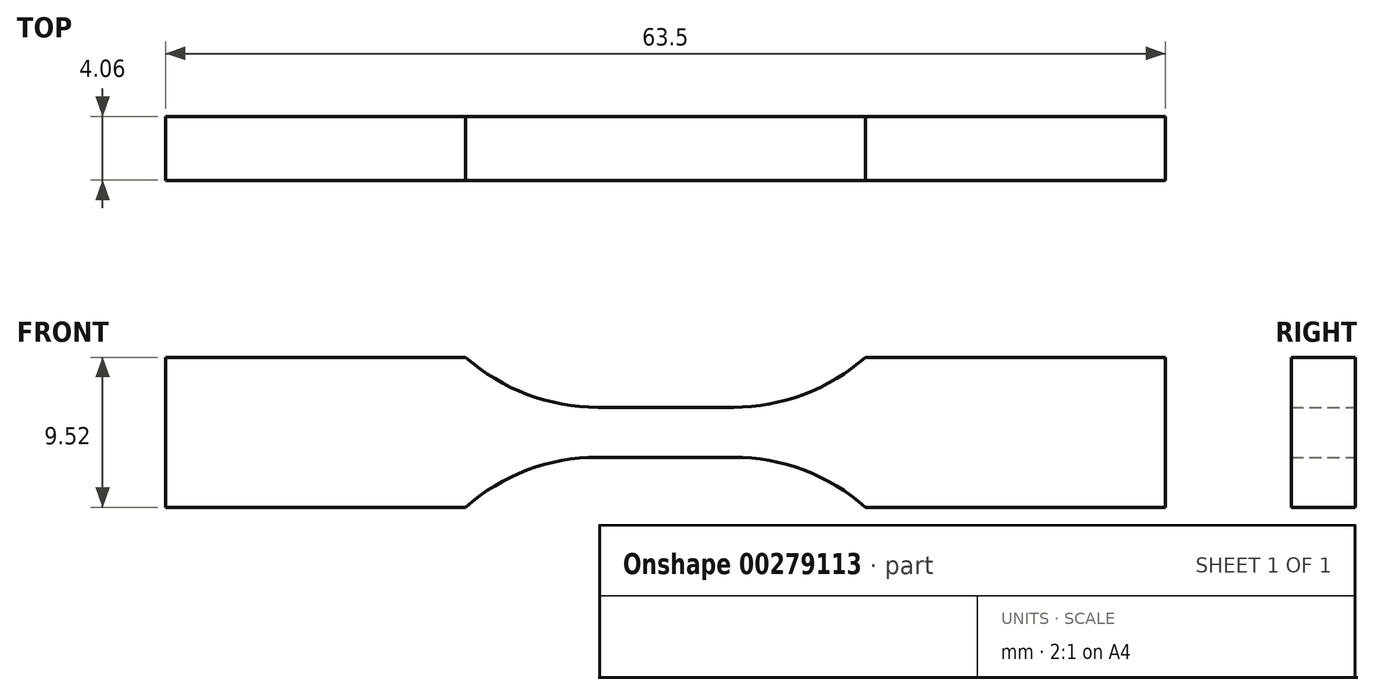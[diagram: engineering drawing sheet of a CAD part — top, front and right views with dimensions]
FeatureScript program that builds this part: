
annotation { "Feature Type Name" : "Feature", "Feature Type Description" : "" }
export const myFeature = defineFeature(function(context is Context, id is Id, definition is map)
    precondition{}
    {
        {
            var Q0;
            Q0=qCreatedBy(makeId("Front.planeOp"),FACE);
            var sketch = newSketch(context, id + "F0", { "sketchPlane" : qUnion([Q0])});
            skLineSegment(sketch, "E0", {"start": v(0, 1.59) * mm, "end": v(4.3, 1.59) * mm});
            skArc(sketch, "E1", {"start": v(4.3, 1.59) * mm, "mid": v(8.79, 2.4) * mm, "end": v(12.7, 4.76) * mm});
            skLineSegment(sketch, "E2", {"start": v(12.7, 4.76) * mm, "end": v(31.75, 4.76) * mm});
            skLineSegment(sketch, "E3", {"start": v(31.75, 4.76) * mm, "end": v(31.75, 0) * mm});
            skLineSegment(sketch, "E4.MirrorCS", {"start": v(0, -1.59) * mm, "end": v(4.3, -1.59) * mm});
            skLineSegment(sketch, "E5.MirrorCS", {"start": v(31.75, -4.76) * mm, "end": v(31.75, 0) * mm});
            skLineSegment(sketch, "E6.MirrorCS", {"start": v(12.7, -4.76) * mm, "end": v(31.75, -4.76) * mm});
            skArc(sketch, "E7.MirrorCS", {"start": v(4.3, -1.59) * mm, "mid": v(8.79, -2.4) * mm, "end": v(12.7, -4.76) * mm});
            skArc(sketch, "E8.MirrorCS", {"start": v(-4.3, -1.59) * mm, "mid": v(-8.79, -2.4) * mm, "end": v(-12.7, -4.76) * mm});
            skLineSegment(sketch, "E9.MirrorCS", {"start": v(-12.7, -4.76) * mm, "end": v(-31.75, -4.76) * mm});
            skArc(sketch, "E10.MirrorCS", {"start": v(-4.3, 1.59) * mm, "mid": v(-8.79, 2.4) * mm, "end": v(-12.7, 4.76) * mm});
            skLineSegment(sketch, "E11.MirrorCS", {"start": v(-12.7, 4.76) * mm, "end": v(-31.75, 4.76) * mm});
            skLineSegment(sketch, "E12.MirrorCS", {"start": v(-31.75, -4.76) * mm, "end": v(-31.75, 0) * mm});
            skLineSegment(sketch, "E13.MirrorCS", {"start": v(0, -1.59) * mm, "end": v(-4.3, -1.59) * mm});
            skLineSegment(sketch, "E14.MirrorCS", {"start": v(-31.75, 4.76) * mm, "end": v(-31.75, 0) * mm});
            skLineSegment(sketch, "E15.MirrorCS", {"start": v(0, 1.59) * mm, "end": v(-4.3, 1.59) * mm});
            skSolve(sketch);
        }
        {
            var Q0;
            Q0 = qSketchRegion(id + "F0", true);
            extrude(context, id + "F1", {"entities" : qUnion([Q0]), "depth" : 4.06 * mm});
        }
    });
